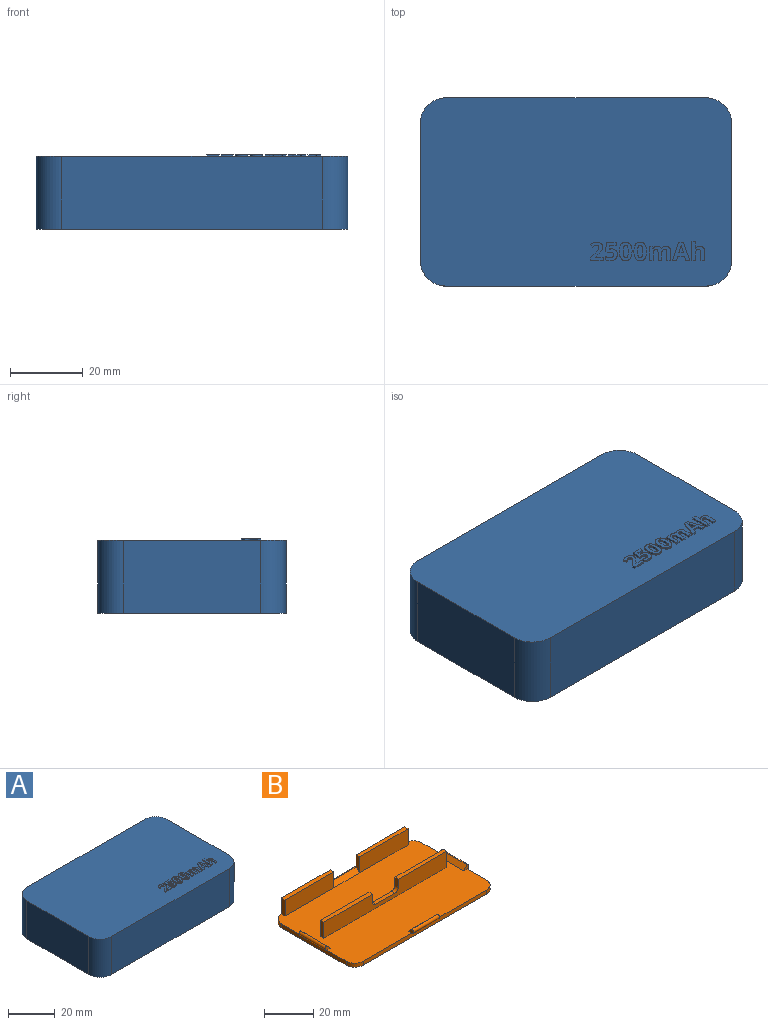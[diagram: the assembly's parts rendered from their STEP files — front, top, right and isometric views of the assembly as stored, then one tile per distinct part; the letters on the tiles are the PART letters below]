
ASSEMBLY  parts=2 mates=1
PART A: 171 faces, bbox 85.4x51.6x20.5 mm
  f0: plane 85.4x51.6mm, normal (0,0,1), area 4279.6mm2, adj f4,f5,f6,f7,f8,f9,f10,f11
  f1: plane 71.4x18mm, normal (0,1,0), area 1251.9mm2, adj f3,f14,f15,f18,f22,f23,f24
  f2: plane 71.4x18mm, normal (0,-1,0), area 1251.9mm2, adj f3,f14,f16,f17,f19,f20,f21
  f3: plane 85.4x51.6mm, normal (0,0,-1), area 511.4mm2, adj f1,f2,f4,f5,f6,f7,f8,f9
  f4: plane 71.4x20mm, normal (0,-1,0), area 1428mm2, adj f0,f3,f8,f11
  f5: plane 37.6x20mm, normal (1,0,0), area 752mm2, adj f0,f3,f8,f9
  f6: plane 71.4x20mm, normal (0,1,0), area 1428mm2, adj f0,f3,f9,f10
  f7: plane 37.6x20mm, normal (-1,0,0), area 752mm2, adj f0,f3,f10,f11
  f8: cylinder r=7mm len=20mm, axis (0,0,1), area 219.9mm2, adj f0,f3,f4,f5
  f9: cylinder r=7mm len=20mm, axis (0,0,-1), area 219.9mm2, adj f0,f3,f5,f6
  f10: cylinder r=7mm len=20mm, axis (0,0,1), area 219.9mm2, adj f0,f3,f6,f7
  f11: cylinder r=7mm len=20mm, axis (0,0,-1), area 219.9mm2, adj f0,f3,f4,f7
  f12: plane 37.6x18mm, normal (-1,0,0), area 676.8mm2, adj f3,f14,f15,f16
  f13: plane 37.6x18mm, normal (1,0,0), area 643.5mm2, adj f3,f14,f17,f18,f25,f26,f27
  f14: plane 81.4x47.6mm, normal (0,0,-1), area 3853.2mm2, adj f1,f2,f12,f13,f15,f16,f17,f18
  f15: cylinder r=5mm len=18mm, axis (0,0,1), area 141.4mm2, adj f1,f3,f12,f14
  f16: cylinder r=5mm len=18mm, axis (0,0,-1), area 141.4mm2, adj f2,f3,f12,f14
  f17: cylinder r=5mm len=18mm, axis (0,0,1), area 141.4mm2, adj f2,f3,f13,f14
  f18: cylinder r=5mm len=18mm, axis (0,0,-1), area 141.4mm2, adj f1,f3,f13,f14
  f19: cylinder r=1.1mm len=15.4mm, axis (1,0,0), area 47mm2, adj f2,f20,f21
  f20: plane 2.16x0.9mm, normal (1,0,0), area 1.5mm2, adj f2,f19
  f21: plane 2.16x0.9mm, normal (-1,0,0), area 1.5mm2, adj f2,f19
  f22: cylinder r=1.1mm len=15.4mm, axis (1,0,0), area 47mm2, adj f1,f23,f24
  f23: plane 2.16x0.9mm, normal (1,0,0), area 1.5mm2, adj f1,f22
  f24: plane 2.16x0.9mm, normal (-1,0,0), area 1.5mm2, adj f1,f22
  f25: cylinder r=1.1mm len=15.4mm, axis (0,1,0), area 47mm2, adj f13,f26,f27
  f26: plane 2.16x0.9mm, normal (0,1,0), area 1.5mm2, adj f13,f25
  f27: plane 2.16x0.9mm, normal (0,-1,0), area 1.5mm2, adj f13,f25
  f28: plane 3.47x0.5mm, normal (0,-1,0), area 1.7mm2, adj f0,f29,f51,f52
  f29: plane 0.88x0.5mm, normal (1,0,0), area 0.4mm2, adj f0,f28,f30,f52
  f30: plane 2.16x0.5mm, normal (0,1,0), area 1.1mm2, adj f0,f29,f31,f52
  f31: plane 0.5x0.05mm, normal (1,0,0), area 0mm2, adj f0,f30,f32,f52
  f32: plane 0.64x0.6mm, normal (0.69,-0.73,0), area 0.4mm2, adj f0,f31,f33,f52
  f33: extruded ~0.9x0.89mm, area 0.6mm2, adj f0,f32,f34,f52
  f34: extruded ~0.62x0.5mm, area 0.4mm2, adj f0,f33,f35,f52
  f35: extruded ~0.64x0.5mm, area 0.3mm2, adj f0,f34,f36,f52
  f36: extruded ~0.7x0.5mm, area 0.4mm2, adj f0,f35,f37,f52
  f37: extruded ~0.55x0.5mm, area 0.4mm2, adj f0,f36,f38,f52
  f38: extruded ~0.82x0.5mm, area 0.4mm2, adj f0,f37,f39,f52
  f39: extruded ~0.64x0.5mm, area 0.3mm2, adj f0,f38,f40,f52
  f40: extruded ~0.53x0.5mm, area 0.3mm2, adj f0,f39,f41,f52
  f41: extruded ~0.61x0.5mm, area 0.4mm2, adj f0,f40,f42,f52
  f42: plane 0.68x0.57mm, normal (-0.76,-0.65,0), area 0.4mm2, adj f0,f41,f43,f52
  f43: extruded ~0.57x0.5mm, area 0.3mm2, adj f0,f42,f44,f52
  f44: extruded ~0.56x0.5mm, area 0.3mm2, adj f0,f43,f45,f52
  f45: extruded ~0.5x0.44mm, area 0.2mm2, adj f0,f44,f46,f52
  f46: extruded ~0.5x0.44mm, area 0.2mm2, adj f0,f45,f47,f52
  f47: extruded ~0.5x0.39mm, area 0.2mm2, adj f0,f46,f48,f52
  f48: extruded ~0.5x0.41mm, area 0.2mm2, adj f0,f47,f49,f52
  f49: extruded ~0.79x0.72mm, area 0.5mm2, adj f0,f48,f50,f52
  f50: plane 1.26x1.24mm, normal (-0.71,0.7,0), area 0.9mm2, adj f0,f49,f51,f52
  f51: plane 0.73x0.5mm, normal (-1,0,0), area 0.4mm2, adj f0,f28,f50,f52
  f52: plane 5.03x3.48mm, normal (0,0,1), area 9.2mm2, adj f28,f29,f30,f31,f32,f33,f34,f35
  f53: extruded ~1.14x0.5mm, area 0.6mm2, adj f0,f54,f72,f73
  f54: extruded ~0.51x0.5mm, area 0.3mm2, adj f0,f53,f55,f73
  f55: plane 0.5x0.12mm, normal (-0.2,0.98,0), area 0.1mm2, adj f0,f54,f56,f73
  f56: plane 0.97x0.5mm, normal (1,-0.09,0), area 0.5mm2, adj f0,f55,f57,f73
  f57: plane 1.77x0.5mm, normal (0,-1,0), area 0.9mm2, adj f0,f56,f58,f73
  f58: plane 0.89x0.5mm, normal (1,0,0), area 0.4mm2, adj f0,f57,f59,f73
  f59: plane 2.69x0.5mm, normal (0,1,0), area 1.3mm2, adj f0,f58,f60,f73
  f60: plane 2.53x0.5mm, normal (-1,0.07,0), area 1.3mm2, adj f0,f59,f61,f73
  f61: plane 0.5x0.42mm, normal (-0.47,-0.88,0), area 0.2mm2, adj f0,f60,f62,f73
  f62: extruded ~0.5x0.35mm, area 0.2mm2, adj f0,f61,f63,f73
  f63: extruded ~0.5x0.4mm, area 0.2mm2, adj f0,f62,f64,f73
  f64: extruded ~0.99x0.75mm, area 0.7mm2, adj f0,f63,f65,f73
  f65: extruded ~0.96x0.79mm, area 0.7mm2, adj f0,f64,f66,f73
  f66: extruded ~0.67x0.5mm, area 0.3mm2, adj f0,f65,f67,f73
  f67: extruded ~0.62x0.5mm, area 0.3mm2, adj f0,f66,f68,f73
  f68: plane 0.91x0.5mm, normal (-1,0,0), area 0.5mm2, adj f0,f67,f69,f73
  f69: extruded ~1.34x0.5mm, area 0.7mm2, adj f0,f68,f70,f73
  f70: extruded ~1.47x0.5mm, area 0.8mm2, adj f0,f69,f71,f73
  f71: extruded ~1.28x0.51mm, area 0.7mm2, adj f0,f70,f72,f73
  f72: extruded ~1.11x0.5mm, area 0.6mm2, adj f0,f53,f71,f73
  f73: plane 5.03x3.31mm, normal (0,0,1), area 9.7mm2, adj f53,f54,f55,f56,f57,f58,f59,f60
  f74: extruded ~1.31x0.5mm, area 0.7mm2, adj f75,f89,f90,f91
  f75: extruded ~1.31x0.5mm, area 0.7mm2, adj f74,f76,f90,f91
  f76: extruded ~0.53x0.5mm, area 0.4mm2, adj f75,f77,f90,f91
  f77: extruded ~0.53x0.5mm, area 0.4mm2, adj f76,f78,f90,f91
  f78: extruded ~1.31x0.5mm, area 0.7mm2, adj f77,f79,f90,f91
  f79: extruded ~1.3x0.5mm, area 0.7mm2, adj f78,f80,f90,f91
  f80: extruded ~0.53x0.5mm, area 0.4mm2, adj f79,f89,f90,f91
  f81: extruded ~1.92x0.5mm, area 1mm2, adj f0,f82,f88,f90
  f82: extruded ~1.91x0.5mm, area 1mm2, adj f0,f81,f83,f90
  f83: extruded ~1.3x0.65mm, area 0.8mm2, adj f0,f82,f84,f90
  f84: extruded ~1.31x0.62mm, area 0.8mm2, adj f0,f83,f85,f90
  f85: extruded ~1.94x0.5mm, area 1mm2, adj f0,f84,f86,f90
  f86: extruded ~1.9x0.5mm, area 1mm2, adj f0,f85,f87,f90
  f87: extruded ~1.29x0.64mm, area 0.8mm2, adj f0,f86,f88,f90
  f88: extruded ~1.31x0.62mm, area 0.8mm2, adj f0,f81,f87,f90
  f89: extruded ~0.53x0.5mm, area 0.4mm2, adj f74,f80,f90,f91
  f90: plane 5.1x3.47mm, normal (0,0,1), area 10.8mm2, adj f74,f75,f76,f77,f78,f79,f80,f81
  f91: plane 3.41x1.38mm, normal (0,0,1), area 4mm2, adj f74,f75,f76,f77,f78,f79,f80,f89
  f92: extruded ~1.31x0.5mm, area 0.7mm2, adj f93,f107,f108,f109
  f93: extruded ~1.31x0.5mm, area 0.7mm2, adj f92,f94,f108,f109
  f94: extruded ~0.53x0.5mm, area 0.4mm2, adj f93,f95,f108,f109
  f95: extruded ~0.53x0.5mm, area 0.4mm2, adj f94,f96,f108,f109
  f96: extruded ~1.31x0.5mm, area 0.7mm2, adj f95,f97,f108,f109
  f97: extruded ~1.3x0.5mm, area 0.7mm2, adj f96,f98,f108,f109
  f98: extruded ~0.53x0.5mm, area 0.4mm2, adj f97,f107,f108,f109
  f99: extruded ~1.92x0.5mm, area 1mm2, adj f0,f100,f106,f108
  f100: extruded ~1.91x0.5mm, area 1mm2, adj f0,f99,f101,f108
  f101: extruded ~1.3x0.65mm, area 0.8mm2, adj f0,f100,f102,f108
  f102: extruded ~1.31x0.62mm, area 0.8mm2, adj f0,f101,f103,f108
  f103: extruded ~1.94x0.5mm, area 1mm2, adj f0,f102,f104,f108
  f104: extruded ~1.9x0.5mm, area 1mm2, adj f0,f103,f105,f108
  f105: extruded ~1.29x0.64mm, area 0.8mm2, adj f0,f104,f106,f108
  f106: extruded ~1.31x0.62mm, area 0.8mm2, adj f0,f99,f105,f108
  f107: extruded ~0.53x0.5mm, area 0.4mm2, adj f92,f98,f108,f109
  f108: plane 5.1x3.47mm, normal (0,0,1), area 10.8mm2, adj f92,f93,f94,f95,f96,f97,f98,f99
  f109: plane 3.41x1.38mm, normal (0,0,1), area 4mm2, adj f92,f93,f94,f95,f96,f97,f98,f107
  f110: plane 1.03x0.5mm, normal (0,-1,0), area 0.5mm2, adj f0,f111,f137,f138
  f111: plane 1.9x0.5mm, normal (1,0,0), area 1mm2, adj f0,f110,f112,f138
  f112: extruded ~0.86x0.5mm, area 0.4mm2, adj f0,f111,f113,f138
  f113: extruded ~0.57x0.5mm, area 0.3mm2, adj f0,f112,f114,f138
  f114: extruded ~0.5x0.43mm, area 0.3mm2, adj f0,f113,f115,f138
  f115: extruded ~0.62x0.5mm, area 0.3mm2, adj f0,f114,f116,f138
  f116: plane 2.21x0.5mm, normal (-1,0,0), area 1.1mm2, adj f0,f115,f117,f138
  f117: plane 1.04x0.5mm, normal (0,-1,0), area 0.5mm2, adj f0,f116,f118,f138
  f118: plane 2.47x0.5mm, normal (1,0,0), area 1.2mm2, adj f0,f117,f119,f138
  f119: extruded ~1.06x0.5mm, area 0.6mm2, adj f0,f118,f120,f138
  f120: extruded ~0.98x0.5mm, area 0.5mm2, adj f0,f119,f121,f138
  f121: extruded ~0.67x0.5mm, area 0.3mm2, adj f0,f120,f122,f138
  f122: extruded ~0.5x0.45mm, area 0.3mm2, adj f0,f121,f123,f138
  f123: plane 0.5x0.09mm, normal (0,1,0), area 0mm2, adj f0,f122,f124,f138
  f124: extruded ~1.15x0.56mm, area 0.7mm2, adj f0,f123,f125,f138
  f125: extruded ~0.66x0.5mm, area 0.3mm2, adj f0,f124,f126,f138
  f126: extruded ~0.5x0.44mm, area 0.3mm2, adj f0,f125,f127,f138
  f127: plane 0.5x0.06mm, normal (0,1,0), area 0mm2, adj f0,f126,f128,f138
  f128: plane 0.5x0.49mm, normal (0.96,0.28,0), area 0.3mm2, adj f0,f127,f129,f138
  f129: plane 0.79x0.5mm, normal (0,1,0), area 0.4mm2, adj f0,f128,f130,f138
  f130: plane 3.79x0.5mm, normal (-1,0,0), area 1.9mm2, adj f0,f129,f131,f138
  f131: plane 1.03x0.5mm, normal (0,-1,0), area 0.5mm2, adj f0,f130,f132,f138
  f132: plane 1.78x0.5mm, normal (1,0,0), area 0.9mm2, adj f0,f131,f133,f138
  f133: extruded ~0.96x0.5mm, area 0.5mm2, adj f0,f132,f134,f138
  f134: extruded ~0.58x0.5mm, area 0.3mm2, adj f0,f133,f135,f138
  f135: extruded ~0.5x0.43mm, area 0.3mm2, adj f0,f134,f136,f138
  f136: extruded ~0.62x0.5mm, area 0.3mm2, adj f0,f135,f137,f138
  f137: plane 2.21x0.5mm, normal (-1,0,0), area 1.1mm2, adj f0,f110,f136,f138
  f138: plane 5.76x3.86mm, normal (0,0,1), area 13.6mm2, adj f110,f111,f112,f113,f114,f115,f116,f117
  f139: extruded ~1.81x0.56mm, area 0.9mm2, adj f140,f150,f151,f152
  f140: plane 1.29x0.5mm, normal (0,1,0), area 0.6mm2, adj f139,f141,f151,f152
  f141: extruded ~2.15x0.64mm, area 1.1mm2, adj f140,f150,f151,f152
  f142: plane 1.18x0.5mm, normal (-0.96,-0.29,0), area 0.6mm2, adj f0,f143,f149,f151
  f143: plane 1.13x0.5mm, normal (0,-1,0), area 0.6mm2, adj f0,f142,f144,f151
  f144: plane 4.98x1.76mm, normal (0.94,0.33,0), area 2.6mm2, adj f0,f143,f145,f151
  f145: plane 1.28x0.5mm, normal (0,1,0), area 0.6mm2, adj f0,f144,f146,f151
  f146: plane 4.98x1.75mm, normal (-0.94,0.33,0), area 2.6mm2, adj f0,f145,f147,f151
  f147: plane 1.13x0.5mm, normal (0,-1,0), area 0.6mm2, adj f0,f146,f148,f151
  f148: plane 1.18x0.5mm, normal (0.96,-0.29,0), area 0.6mm2, adj f0,f147,f149,f151
  f149: plane 1.81x0.5mm, normal (0,-1,0), area 0.9mm2, adj f0,f142,f148,f151
  f150: extruded ~0.5x0.33mm, area 0.2mm2, adj f139,f141,f151,f152
  f151: plane 4.98x4.79mm, normal (0,0,1), area 11.2mm2, adj f139,f140,f141,f142,f143,f144,f145,f146
  f152: plane 2.15x1.29mm, normal (0,0,1), area 1.4mm2, adj f139,f140,f141,f150
  f153: plane 1.03x0.5mm, normal (0,-1,0), area 0.5mm2, adj f0,f154,f169,f170
  f154: plane 2.47x0.5mm, normal (1,0,0), area 1.2mm2, adj f0,f153,f155,f170
  f155: extruded ~1.03x0.5mm, area 0.6mm2, adj f0,f154,f156,f170
  f156: extruded ~1.01x0.5mm, area 0.6mm2, adj f0,f155,f157,f170
  f157: extruded ~1.1x0.56mm, area 0.6mm2, adj f0,f156,f158,f170
  f158: plane 0.5x0.05mm, normal (0,1,0), area 0mm2, adj f0,f157,f159,f170
  f159: plane 0.5x0.31mm, normal (1,-0.08,0), area 0.2mm2, adj f0,f158,f160,f170
  f160: extruded ~0.59x0.5mm, area 0.3mm2, adj f0,f159,f161,f170
  f161: plane 1.08x0.5mm, normal (1,0,0), area 0.5mm2, adj f0,f160,f162,f170
  f162: plane 1.03x0.5mm, normal (0,1,0), area 0.5mm2, adj f0,f161,f163,f170
  f163: plane 5.28x0.5mm, normal (-1,0,0), area 2.6mm2, adj f0,f162,f164,f170
  f164: plane 1.03x0.5mm, normal (0,-1,0), area 0.5mm2, adj f0,f163,f165,f170
  f165: plane 1.78x0.5mm, normal (1,0,0), area 0.9mm2, adj f0,f164,f166,f170
  f166: extruded ~0.96x0.5mm, area 0.5mm2, adj f0,f165,f167,f170
  f167: extruded ~0.63x0.5mm, area 0.4mm2, adj f0,f166,f168,f170
  f168: extruded ~0.82x0.61mm, area 0.6mm2, adj f0,f167,f169,f170
  f169: plane 2.21x0.5mm, normal (-1,0,0), area 1.1mm2, adj f0,f153,f168,f170
  f170: plane 5.28x3.5mm, normal (0,0,1), area 10.4mm2, adj f153,f154,f155,f156,f157,f158,f159,f160
PART B: 45 faces, bbox 83x49.2x10 mm
  f0: plane 28x2mm, normal (0,0,1), area 56mm2, adj f1,f36,f37,f42
  f1: plane 71x8mm, normal (0,-1,0), area 479.7mm2, adj f0,f2,f37,f38,f39,f40,f41,f42
  f2: plane 81x47.2mm, normal (0,0,1), area 3427.7mm2, adj f1,f3,f4,f6,f8,f9,f10,f11
  f3: plane 71x2mm, normal (0,-1,0), area 142mm2, adj f2,f7,f8,f11,f22
  f4: plane 37.2x2mm, normal (1,0,0), area 74.4mm2, adj f2,f7,f8,f9,f20
  f5: plane 71x10mm, normal (0,1,0), area 590mm2, adj f7,f9,f10,f18,f19,f23,f28,f29
  f6: plane 37.2x2mm, normal (-1,0,0), area 74.4mm2, adj f2,f7,f10,f11,f21
  f7: plane 81x47.2mm, normal (0,0,-1), area 3801.7mm2, adj f3,f4,f5,f6,f8,f9,f10,f11
  f8: cylinder r=5mm len=5mm, axis (0,0,1), area 15.7mm2, adj f2,f3,f4,f7
  f9: cylinder r=5mm len=5mm, axis (0,0,-1), area 15.7mm2, adj f2,f4,f5,f7
  f10: cylinder r=5mm len=5mm, axis (0,0,1), area 15.7mm2, adj f2,f5,f6,f7
  f11: cylinder r=5mm len=5mm, axis (0,0,-1), area 15.7mm2, adj f2,f3,f6,f7
  f12: plane 3x2mm, normal (0,-1,0), area 3.6mm2, adj f2,f21,f26
  f13: plane 3x2mm, normal (0,1,0), area 3.6mm2, adj f2,f21,f26
  f14: plane 3x2mm, normal (-1,0,0), area 3.6mm2, adj f2,f22,f25
  f15: plane 3x2mm, normal (1,0,0), area 3.6mm2, adj f2,f22,f25
  f16: plane 3x2mm, normal (0,-1,0), area 3.6mm2, adj f2,f20,f27
  f17: plane 3x2mm, normal (0,1,0), area 3.6mm2, adj f2,f20,f27
  f18: plane 2x1mm, normal (-1,0,0), area 1.6mm2, adj f5,f23
  f19: plane 2x1mm, normal (1,0,0), area 1.6mm2, adj f5,f23
  f20: cylinder r=1mm len=15mm, axis (0,-1,0), area 47.1mm2, adj f4,f16,f17,f27
  f21: cylinder r=1mm len=15mm, axis (0,-1,0), area 47.1mm2, adj f6,f12,f13,f26
  f22: cylinder r=1mm len=15mm, axis (1,0,0), area 47.1mm2, adj f3,f14,f15,f25
  f23: cylinder r=1mm len=15mm, axis (1,0,0), area 47.1mm2, adj f5,f18,f19,f24
  f24: plane 15x2mm, normal (0,-0.71,0.71), area 42.4mm2, adj f2,f23,f28,f34
  f25: plane 15x2mm, normal (0,0.71,0.71), area 42.4mm2, adj f2,f14,f15,f22
  f26: plane 15x2mm, normal (0.71,0,0.71), area 42.4mm2, adj f2,f12,f13,f21
  f27: plane 15x2mm, normal (-0.71,0,0.71), area 42.4mm2, adj f2,f16,f17,f20
  f28: plane 8x2mm, normal (1,0,0), area 14mm2, adj f5,f24,f30,f31
  f29: plane 8x2mm, normal (-1,0,0), area 16mm2, adj f2,f5,f30,f31
  f30: plane 28x8mm, normal (0,-1,0), area 224mm2, adj f2,f28,f29,f31
  f31: plane 28x2mm, normal (0,0,1), area 56mm2, adj f5,f28,f29,f30
  f32: plane 28x8mm, normal (0,-1,0), area 224mm2, adj f2,f33,f34,f35
  f33: plane 8x2mm, normal (1,0,0), area 16mm2, adj f2,f5,f32,f35
  f34: plane 8x2mm, normal (-1,0,0), area 14mm2, adj f5,f24,f32,f35
  f35: plane 28x2mm, normal (0,0,1), area 56mm2, adj f5,f32,f33,f34
  f36: plane 71x8mm, normal (0,1,0), area 479.7mm2, adj f0,f2,f37,f38,f39,f40,f41,f42
  f37: plane 8x2mm, normal (-1,0,0), area 16mm2, adj f0,f1,f2,f36
  f38: plane 8x2mm, normal (1,0,0), area 16mm2, adj f1,f2,f36,f39
  f39: plane 28x2mm, normal (0,0,1), area 56mm2, adj f1,f36,f38,f40
  f40: plane 4x2mm, normal (-1,0,0), area 8mm2, adj f1,f36,f39,f43
  f41: plane 11x2mm, normal (0,0,1), area 22mm2, adj f1,f36,f43,f44
  f42: plane 4x2mm, normal (1,0,0), area 8mm2, adj f0,f1,f36,f44
  f43: cylinder r=2mm len=2mm, axis (0,-1,0), area 6.3mm2, adj f1,f36,f40,f41
  f44: cylinder r=2mm len=2mm, axis (0,1,0), area 6.3mm2, adj f1,f36,f41,f42
PLACE A at identity
PLACE B at identity
MATE fastened A.f3 <-> B.f7  axis (0,0,-1) through (0,0,0)mm
